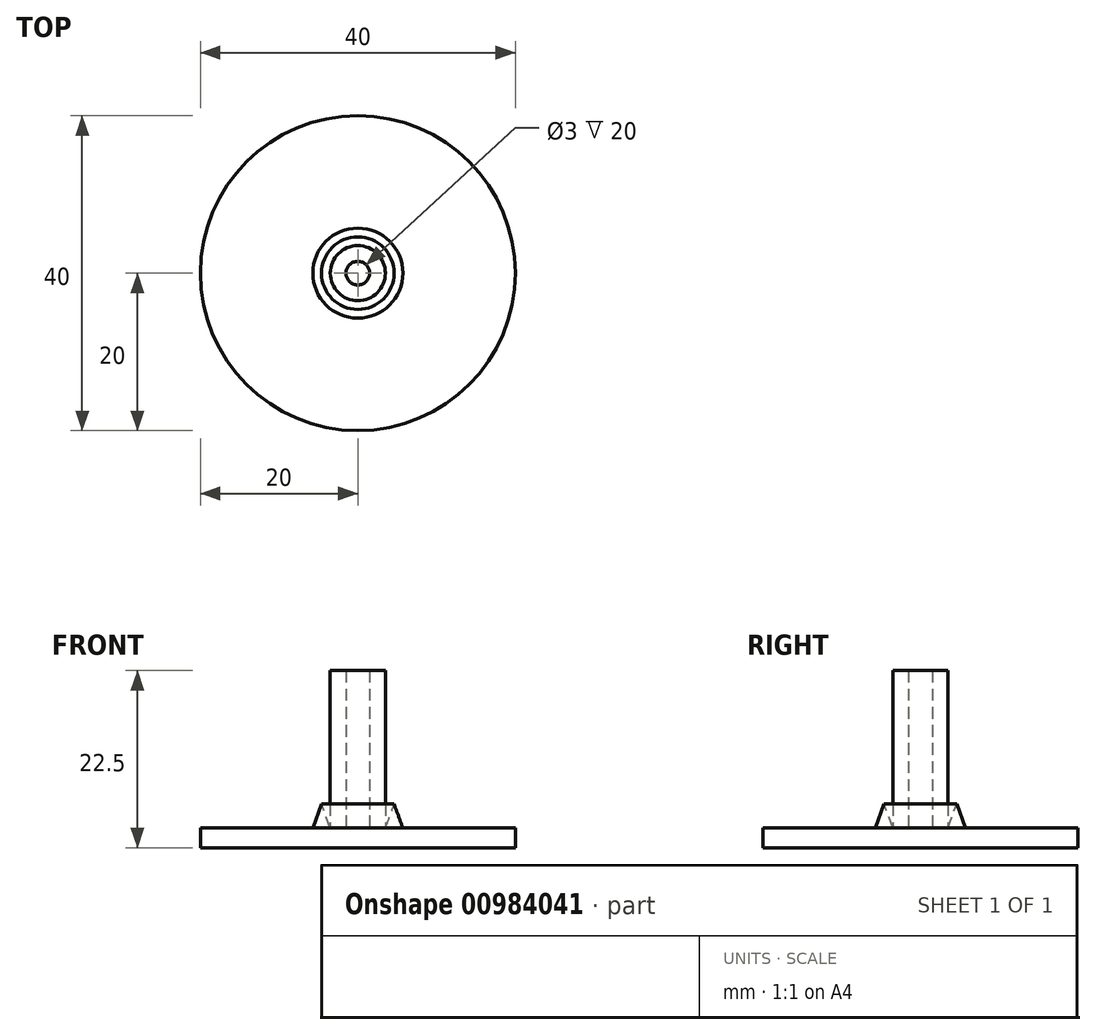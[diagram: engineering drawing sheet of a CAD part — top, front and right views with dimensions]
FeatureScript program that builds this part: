
annotation { "Feature Type Name" : "Feature", "Feature Type Description" : "" }
export const myFeature = defineFeature(function(context is Context, id is Id, definition is map)
    precondition{}
    {
        {
            var Q0;
            Q0=qCreatedBy(makeId("Top.planeOp"),FACE);
            var sketch = newSketch(context, id + "F0", { "sketchPlane" : qUnion([Q0])});
            skCircle(sketch, "E0", {"center": v(0, 0) * mm, "radius": 20 * mm});
            skSolve(sketch);
        }
        {
            var Q0;
            Q0=makeQuery(id+"F0.imprint","IMPRINT",FACE,{"disambiguationData":[TD([[makeQuery(id+"F0.imprint","IMPRINT",EDGE,{"derivedFrom":sQuery(id+"F0.wireOp",EDGE,"E0")}),1.0]])]});
            extrude(context, id + "F1", {"entities" : qUnion([Q0]), "depth" : 2.5 * mm, "offsetDistance" : 25 * mm});
        }
        {
            var Q0;
            Q0=makeQuery(id+"F1.opExtrude","CAP_FACE",FACE,{"disambiguationData":[OSD([sQuery(id+"F0.wireOp",EDGE,"E0")])],"isStart":false});
            var sketch = newSketch(context, id + "F2", { "sketchPlane" : qUnion([Q0])});
            skCircle(sketch, "E1", {"center": v(0, 0) * mm, "radius": 1.5 * mm});
            skCircle(sketch, "E2", {"center": v(0, 0) * mm, "radius": 3.5 * mm});
            skSolve(sketch);
        }
        {
            var Q0;
            Q0 = qSketchRegion(id + "F2", true);
            extrude(context, id + "F3", {"entities" : qUnion([Q0]), "operationType" : NewBodyOperationType.ADD, "depth" : 20 * mm, "offsetDistance" : 25 * mm});
        }
        {
            var Q0;
            {var subQ0=sQuery(id+"F0.wireOp",EDGE,"E0");Q0=makeQuery(id+"F3.boolean.opBoolean","SPLIT",FACE,{"disambiguationData":[TD([makeQuery(id+"F1.opExtrude","SWEPT_FACE",FACE,{"disambiguationData":[OSD([subQ0])]})])],"derivedFrom":makeQuery(id+"F1.opExtrude","CAP_FACE",FACE,{"disambiguationData":[OSD([subQ0])],"isStart":false})});}
            var sketch = newSketch(context, id + "F4", { "sketchPlane" : qUnion([Q0])});
            skCircle(sketch, "E3", {"center": v(0, 0) * mm, "radius": 5.72 * mm});
            skCircle(sketch, "E4", {"center": v(0, 0) * mm, "radius": 10.16 * mm});
            skCircle(sketch, "E5", {"center": v(0, 0) * mm, "radius": 15.62 * mm});
            skSolve(sketch);
        }
        {
            var Q0;
            Q0=makeQuery(id+"F4.imprint","IMPRINT",FACE,{"disambiguationData":[TD([[makeQuery(id+"F4.imprint","IMPRINT",EDGE,{"derivedFrom":makeQuery(id+"F3.opExtrude","CAP_EDGE",EDGE,{"disambiguationData":[OSD([sQuery(id+"F2.wireOp",EDGE,"E2")])],"isStart":true})}),1.0]])]});
            var Q1;
            Q1=makeQuery(id+"F4.imprint","IMPRINT",FACE,{"disambiguationData":[TD([[makeQuery(id+"F4.imprint","IMPRINT",EDGE,{"derivedFrom":sQuery(id+"F4.wireOp",EDGE,"E3")}),1.0]])]});
            extrude(context, id + "F5", {"entities" : qUnion([Q0, Q1]), "operationType" : NewBodyOperationType.ADD, "depth" : 5 * mm, "offsetDistance" : 25 * mm, "hasDraft" : true, "draftAngle" : 20 * degree, "draftPullDirection" : true});
        }
    });
